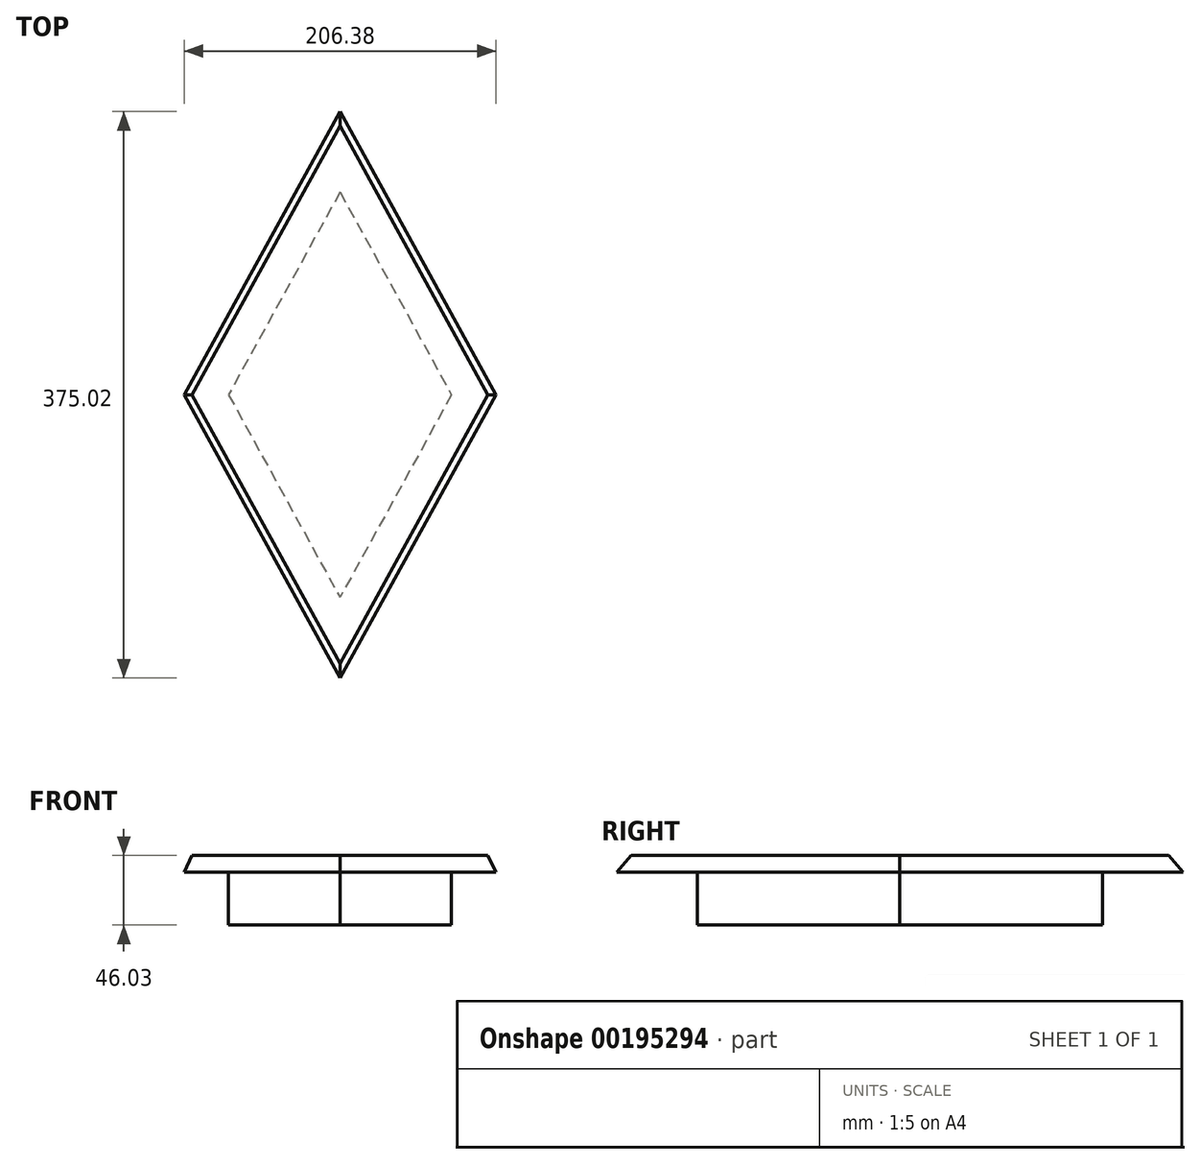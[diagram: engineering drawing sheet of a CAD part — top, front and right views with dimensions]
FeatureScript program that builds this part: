
annotation { "Feature Type Name" : "Feature", "Feature Type Description" : "" }
export const myFeature = defineFeature(function(context is Context, id is Id, definition is map)
    precondition{}
    {
        {
            var Q0;
            Q0=qCreatedBy(makeId("Top.planeOp"),FACE);
            var sketch = newSketch(context, id + "F0", { "sketchPlane" : qUnion([Q0])});
            skLineSegment(sketch, "E0", {"start": v(0, 134.14) * mm, "end": v(73.82, 0) * mm});
            skLineSegment(sketch, "E1", {"start": v(73.82, 0) * mm, "end": v(0, -134.14) * mm});
            skLineSegment(sketch, "E2", {"start": v(0, -134.14) * mm, "end": v(0, 134.14) * mm});
            skPoint(sketch, "E3.start.orphan", {"position": v(-73.82, 0) * mm});
            skLineSegment(sketch, "E4.MirrorCS", {"start": v(-73.82, 0) * mm, "end": v(0, -134.14) * mm});
            skLineSegment(sketch, "E5.MirrorCS", {"start": v(0, 134.14) * mm, "end": v(-73.82, 0) * mm});
            skLineSegment(sketch, "E6", {"start": v(0, -187.51) * mm, "end": v(103.19, 0) * mm});
            skLineSegment(sketch, "E7", {"start": v(103.19, 0) * mm, "end": v(0, 187.51) * mm});
            skLineSegment(sketch, "E8.MirrorCS", {"start": v(0, -187.51) * mm, "end": v(-103.19, 0) * mm});
            skLineSegment(sketch, "E9.MirrorCS", {"start": v(-103.19, 0) * mm, "end": v(0, 187.51) * mm});
            skSolve(sketch);
        }
        {
            var Q0;
            Q0=makeQuery(id+"F0.imprint","IMPRINT",FACE,{"disambiguationData":[TD([[makeQuery(id+"F0.imprint","IMPRINT",EDGE,{"derivedFrom":sQuery(id+"F0.wireOp",EDGE,"E2")}),1.0]])]});
            var Q1;
            Q1=makeQuery(id+"F0.imprint","IMPRINT",FACE,{"disambiguationData":[TD([[makeQuery(id+"F0.imprint","IMPRINT",EDGE,{"derivedFrom":sQuery(id+"F0.wireOp",EDGE,"E0")}),-1.0]])]});
            extrude(context, id + "F1", {"entities" : qUnion([Q0, Q1]), "oppositeDirection" : true, "depth" : 34.92 * mm});
        }
        {
            var Q0;
            Q0 = qSketchRegion(id + "F0", true);
            var Q1;
            Q1=makeQuery(id+"F1.opExtrude","CAP_FACE",FACE,{"disambiguationData":[OSD([sQuery(id+"F0.wireOp",EDGE,"E0"),sQuery(id+"F0.wireOp",EDGE,"E1"),sQuery(id+"F0.wireOp",EDGE,"E4.MirrorCS"),sQuery(id+"F0.wireOp",EDGE,"E5.MirrorCS")])],"isStart":true});
            extrude(context, id + "F2", {"entities" : qUnion([Q0, Q1]), "operationType" : NewBodyOperationType.ADD, "depth" : 11.1 * mm});
        }
        {
            var Q0;
            Q0=makeQuery(id+"F2.opExtrude","CAP_EDGE",EDGE,{"disambiguationData":[OSD([sQuery(id+"F0.wireOp",EDGE,"E8.MirrorCS")])],"isStart":false});
            var Q1;
            Q1=makeQuery(id+"F2.opExtrude","CAP_EDGE",EDGE,{"disambiguationData":[OSD([sQuery(id+"F0.wireOp",EDGE,"E9.MirrorCS")])],"isStart":false});
            var Q2;
            Q2=makeQuery(id+"F2.opExtrude","CAP_EDGE",EDGE,{"disambiguationData":[OSD([sQuery(id+"F0.wireOp",EDGE,"E7")])],"isStart":false});
            var Q3;
            Q3=makeQuery(id+"F2.opExtrude","CAP_EDGE",EDGE,{"disambiguationData":[OSD([sQuery(id+"F0.wireOp",EDGE,"E6")])],"isStart":false});
            chamfer(context, id + "F3", {"entities" : qUnion([Q0, Q1, Q2, Q3]), "chamferType" : ChamferType.OFFSET_ANGLE, "width" : 11.1 * mm, "oppositeDirection" : false, "angle" : 22.5 * degree, "tangentPropagation" : true});
        }
    });
